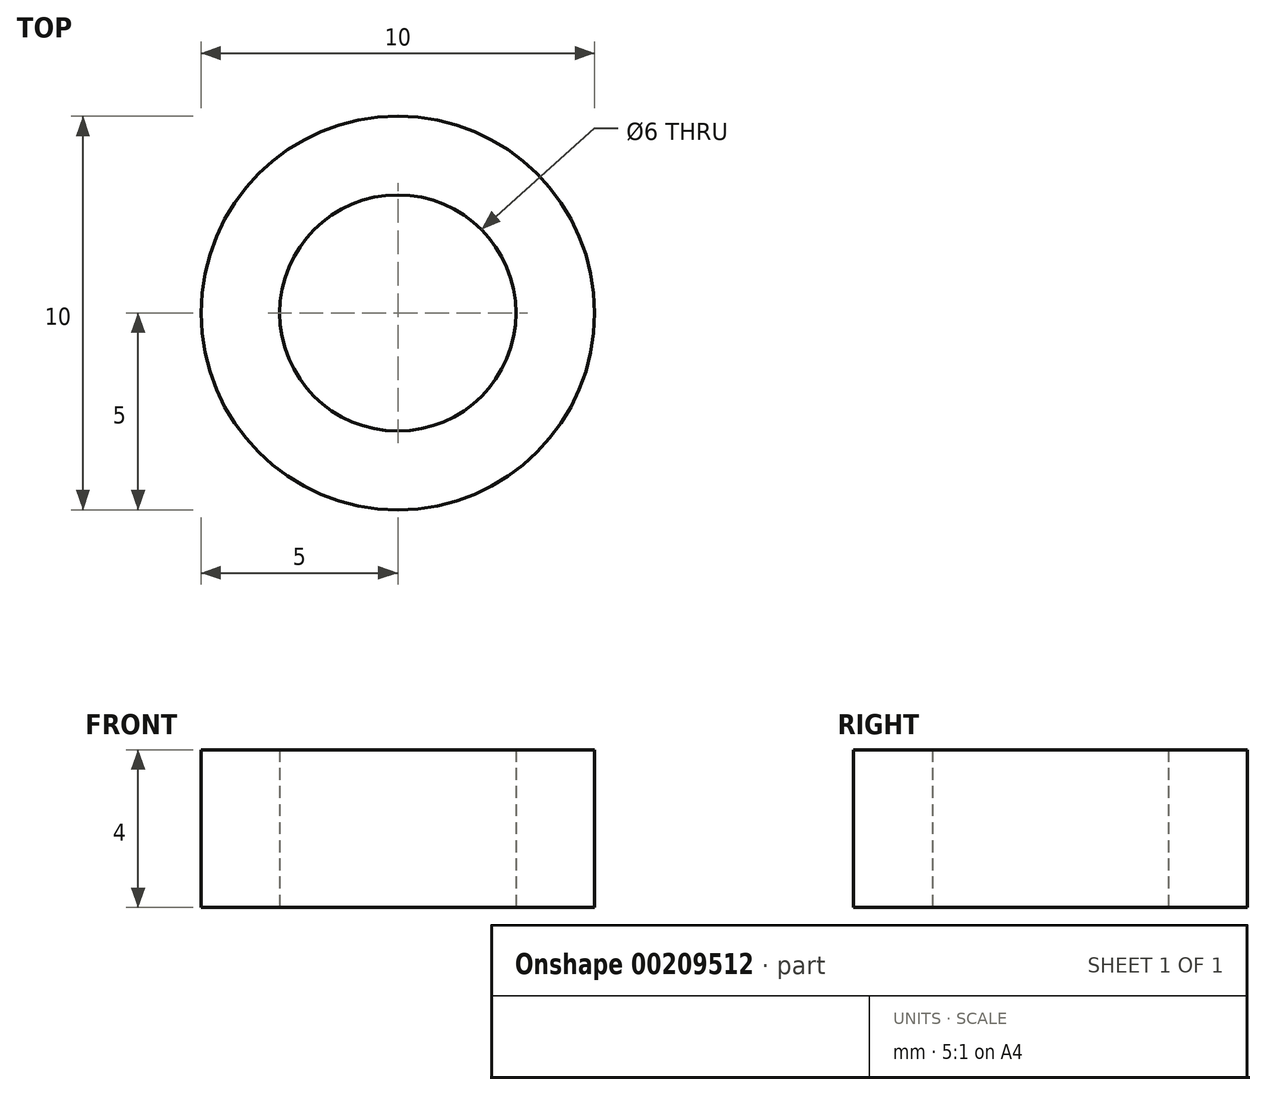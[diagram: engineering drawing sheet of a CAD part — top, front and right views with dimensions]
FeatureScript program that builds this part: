
annotation { "Feature Type Name" : "Feature", "Feature Type Description" : "" }
export const myFeature = defineFeature(function(context is Context, id is Id, definition is map)
    precondition{}
    {
        {
            var Q0;
            Q0=qCreatedBy(makeId("Top.planeOp"),FACE);
            var sketch = newSketch(context, id + "F0", { "sketchPlane" : qUnion([Q0])});
            skCircle(sketch, "E0", {"center": v(0, 0) * mm, "radius": 5 * mm});
            skCircle(sketch, "E1", {"center": v(0, 0) * mm, "radius": 3 * mm});
            skSolve(sketch);
        }
        {
            var Q0;
            Q0=makeQuery(id+"F0.imprint","IMPRINT",FACE,{"disambiguationData":[TD([[makeQuery(id+"F0.imprint","IMPRINT",EDGE,{"derivedFrom":sQuery(id+"F0.wireOp",EDGE,"E0")}),1.0]])]});
            extrude(context, id + "F1", {"entities" : qUnion([Q0]), "depth" : 4 * mm});
        }
    });
